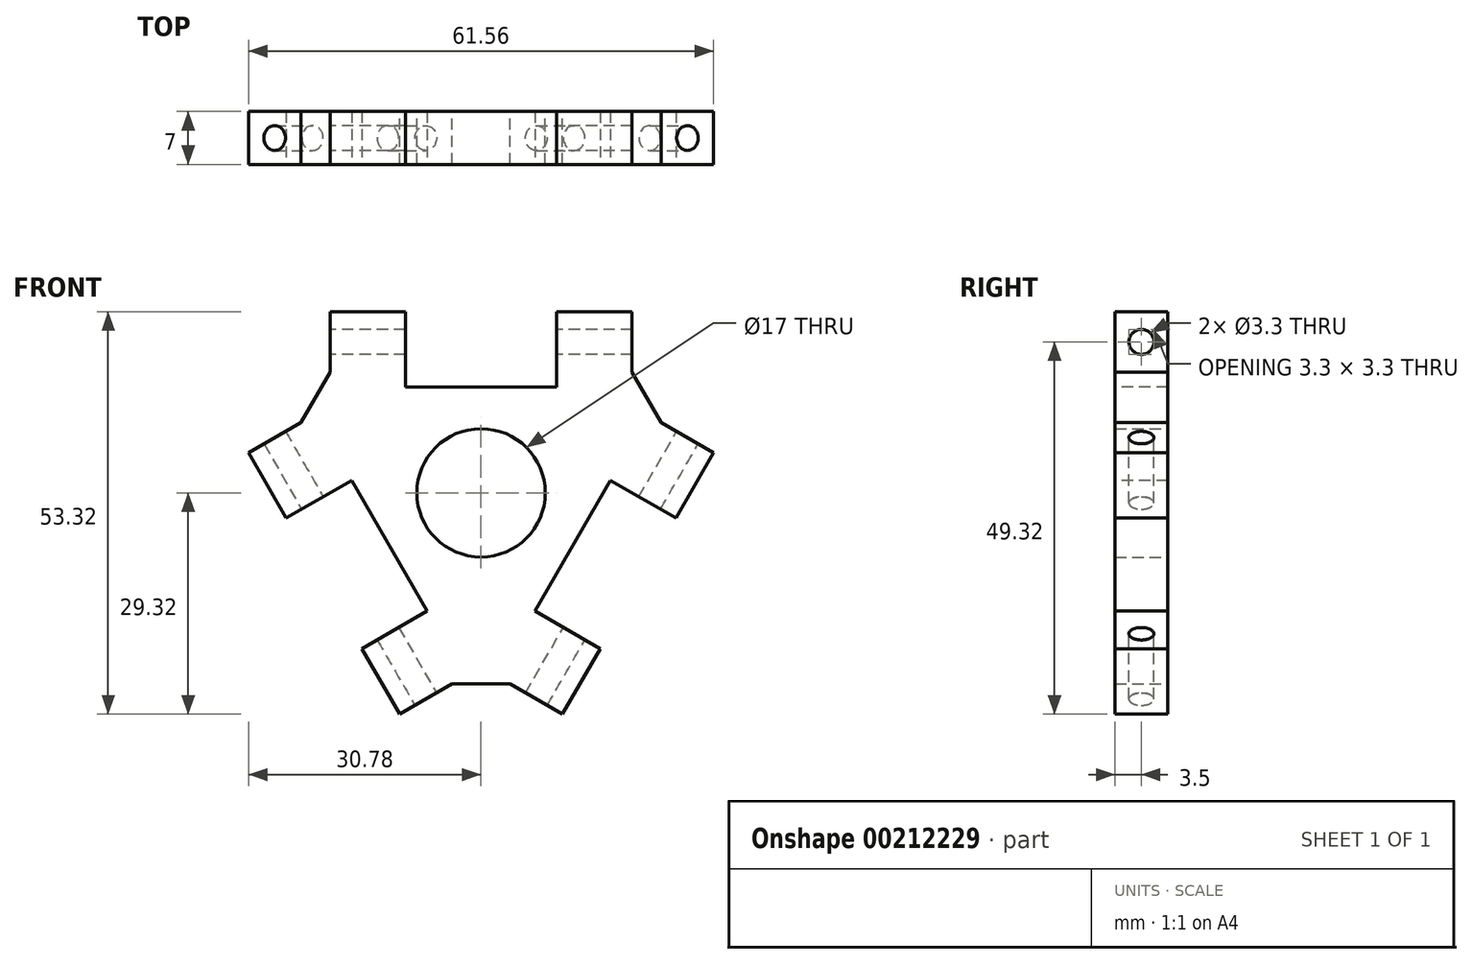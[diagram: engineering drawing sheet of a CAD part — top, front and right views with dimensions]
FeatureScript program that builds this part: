
annotation { "Feature Type Name" : "Feature", "Feature Type Description" : "" }
export const myFeature = defineFeature(function(context is Context, id is Id, definition is map)
    precondition{}
    {
        {
            var Q0;
            Q0=qCreatedBy(makeId("Front.planeOp"),FACE);
            var sketch = newSketch(context, id + "F0", { "sketchPlane" : qUnion([Q0])});
            skCircle(sketch, "E0", {"center": v(0, 0) * mm, "radius": 8.5 * mm});
            skCircle(sketch, "E1", {"center": v(0, 0) * mm, "radius": 16 * mm});
            skLineSegment(sketch, "E2", {"start": v(0, 0) * mm, "end": v(0, 20) * mm});
            skLineSegment(sketch, "E3", {"start": v(0, 0) * mm, "end": v(-17.32, -10) * mm});
            skLineSegment(sketch, "E4", {"start": v(0, 0) * mm, "end": v(17.32, -10) * mm});
            skPoint(sketch, "E5", {"position": v(0, 16) * mm});
            skPoint(sketch, "E6", {"position": v(-13.86, -8) * mm});
            skPoint(sketch, "E7", {"position": v(13.86, -8) * mm});
            skPoint(sketch, "E8", {"position": v(0, 20) * mm});
            skLineSegment(sketch, "E9.bottom", {"start": v(20, 16) * mm, "end": v(-20, 16) * mm});
            skLineSegment(sketch, "E9.top", {"start": v(20, 24) * mm, "end": v(-20, 24) * mm});
            skLineSegment(sketch, "E9.left", {"start": v(20, 16) * mm, "end": v(20, 24) * mm});
            skLineSegment(sketch, "E9.right", {"start": v(-20, 16) * mm, "end": v(-20, 24) * mm});
            skPoint(sketch, "E10", {"position": v(-17.32, -10) * mm});
            skPoint(sketch, "E11", {"position": v(17.32, -10) * mm});
            skLineSegment(sketch, "E12", {"start": v(-13.86, -8) * mm, "end": v(-23.86, 9.32) * mm});
            skLineSegment(sketch, "E13", {"start": v(-13.86, -8) * mm, "end": v(-3.86, -25.32) * mm});
            skLineSegment(sketch, "E14", {"start": v(-3.86, -25.32) * mm, "end": v(-10.78, -29.32) * mm});
            skLineSegment(sketch, "E15", {"start": v(-10.78, -29.32) * mm, "end": v(-30.78, 5.32) * mm});
            skLineSegment(sketch, "E16", {"start": v(-30.78, 5.32) * mm, "end": v(-23.86, 9.32) * mm});
            skLineSegment(sketch, "E17", {"start": v(13.86, -8) * mm, "end": v(23.86, 9.32) * mm});
            skLineSegment(sketch, "E18", {"start": v(23.86, 9.32) * mm, "end": v(30.78, 5.32) * mm});
            skLineSegment(sketch, "E19", {"start": v(30.78, 5.32) * mm, "end": v(10.78, -29.32) * mm});
            skLineSegment(sketch, "E20", {"start": v(10.78, -29.32) * mm, "end": v(3.86, -25.32) * mm});
            skLineSegment(sketch, "E21", {"start": v(20, 16) * mm, "end": v(23.86, 9.32) * mm});
            skLineSegment(sketch, "E22", {"start": v(3.86, -25.32) * mm, "end": v(-3.86, -25.32) * mm});
            skLineSegment(sketch, "E23", {"start": v(-20, 16) * mm, "end": v(-23.86, 9.32) * mm});
            skLineSegment(sketch, "E24", {"start": v(13.86, -8) * mm, "end": v(3.86, -25.32) * mm});
            skSolve(sketch);
        }
        {
            var Q0;
            {var subQ0=sQuery(id+"F0.wireOp",EDGE,"E3");var subQ1=sQuery(id+"F0.wireOp",EDGE,"E0");var subQ2=makeQuery(id+"F0.imprint","INTERSECT",VERTEX,{"derivedFrom":[subQ1,subQ0]});Q0=makeQuery(id+"F0.imprint","IMPRINT",FACE,{"disambiguationData":[TD([[makeQuery(id+"F0.imprint","IMPRINT",EDGE,{"disambiguationData":[TD([[subQ2,1.0]])],"derivedFrom":subQ1}),-1.0]])]});}
            var Q1;
            Q1=makeQuery(id+"F0.imprint","IMPRINT",FACE,{"disambiguationData":[TD([[makeQuery(id+"F0.imprint","IMPRINT",EDGE,{"derivedFrom":sQuery(id+"F0.wireOp",EDGE,"E9.top")}),1.0]])]});
            var Q2;
            {var subQ0=sQuery(id+"F0.wireOp",EDGE,"E12");Q2=makeQuery(id+"F0.imprint","IMPRINT",FACE,{"disambiguationData":[TD([[makeQuery(id+"F0.imprint","IMPRINT",EDGE,{"derivedFrom":subQ0}),-1.0]])]});}
            var Q3;
            Q3=makeQuery(id+"F0.imprint","IMPRINT",FACE,{"disambiguationData":[TD([[makeQuery(id+"F0.imprint","IMPRINT",EDGE,{"derivedFrom":sQuery(id+"F0.wireOp",EDGE,"E12")}),1.0]])]});
            var Q4;
            {var subQ0=sQuery(id+"F0.wireOp",EDGE,"E3");var subQ1=sQuery(id+"F0.wireOp",EDGE,"E0");var subQ2=makeQuery(id+"F0.imprint","INTERSECT",VERTEX,{"derivedFrom":[subQ1,subQ0]});Q4=makeQuery(id+"F0.imprint","IMPRINT",FACE,{"disambiguationData":[TD([[makeQuery(id+"F0.imprint","IMPRINT",EDGE,{"disambiguationData":[TD([[subQ2,-1.0]])],"derivedFrom":subQ1}),-1.0]])]});}
            var Q5;
            {var subQ0=sQuery(id+"F0.wireOp",EDGE,"E13");Q5=makeQuery(id+"F0.imprint","IMPRINT",FACE,{"disambiguationData":[TD([[makeQuery(id+"F0.imprint","IMPRINT",EDGE,{"derivedFrom":subQ0}),1.0]])]});}
            var Q6;
            Q6=makeQuery(id+"F0.imprint","IMPRINT",FACE,{"disambiguationData":[TD([[makeQuery(id+"F0.imprint","IMPRINT",EDGE,{"derivedFrom":sQuery(id+"F0.wireOp",EDGE,"E17")}),-1.0]])]});
            var Q7;
            {var subQ0=sQuery(id+"F0.wireOp",EDGE,"E2");var subQ1=sQuery(id+"F0.wireOp",EDGE,"E0");var subQ2=makeQuery(id+"F0.imprint","INTERSECT",VERTEX,{"derivedFrom":[subQ1,subQ0]});Q7=makeQuery(id+"F0.imprint","IMPRINT",FACE,{"disambiguationData":[TD([[makeQuery(id+"F0.imprint","IMPRINT",EDGE,{"disambiguationData":[TD([[subQ2,1.0]])],"derivedFrom":subQ1}),-1.0]])]});}
            var Q8;
            {var subQ0=sQuery(id+"F0.wireOp",EDGE,"E17");Q8=makeQuery(id+"F0.imprint","IMPRINT",FACE,{"disambiguationData":[TD([[makeQuery(id+"F0.imprint","IMPRINT",EDGE,{"derivedFrom":subQ0}),1.0]])]});}
            extrude(context, id + "F1", {"entities" : qUnion([Q0, Q1, Q2, Q3, Q4, Q5, Q6, Q7, Q8]), "depth" : 7 * mm});
        }
        {
            var Q0;
            Q0=makeQuery(id+"F1.opExtrude","CAP_FACE",FACE,{"disambiguationData":[OSD([sQuery(id+"F0.wireOp",EDGE,"E0"),sQuery(id+"F0.wireOp",EDGE,"E9.top"),sQuery(id+"F0.wireOp",EDGE,"E9.left"),sQuery(id+"F0.wireOp",EDGE,"E9.right"),sQuery(id+"F0.wireOp",EDGE,"E14"),sQuery(id+"F0.wireOp",EDGE,"E15"),sQuery(id+"F0.wireOp",EDGE,"E16"),sQuery(id+"F0.wireOp",EDGE,"E18"),sQuery(id+"F0.wireOp",EDGE,"E19"),sQuery(id+"F0.wireOp",EDGE,"E20"),sQuery(id+"F0.wireOp",EDGE,"E21"),sQuery(id+"F0.wireOp",EDGE,"E22"),sQuery(id+"F0.wireOp",EDGE,"E23")])],"isStart":false});
            var sketch = newSketch(context, id + "F2", { "sketchPlane" : qUnion([Q0])});
            skLineSegment(sketch, "E25.bottom", {"start": v(10, 14) * mm, "end": v(-10, 14) * mm});
            skLineSegment(sketch, "E25.top", {"start": v(10, 34) * mm, "end": v(-10, 34) * mm});
            skLineSegment(sketch, "E25.left", {"start": v(10, 14) * mm, "end": v(10, 34) * mm});
            skLineSegment(sketch, "E25.right", {"start": v(-10, 14) * mm, "end": v(-10, 34) * mm});
            skPoint(sketch, "E25.middle", {"position": v(0, 24) * mm});
            skSolve(sketch);
        }
        {
            var Q0;
            {var subQ0=sQuery(id+"F2.wireOp",EDGE,"E25.bottom");Q0=makeQuery(id+"F2.imprint","IMPRINT",FACE,{"disambiguationData":[TD([[makeQuery(id+"F2.imprint","IMPRINT",EDGE,{"derivedFrom":subQ0}),-1.0]])]});}
            extrude(context, id + "F3", {"entities" : qUnion([Q0]), "operationType" : NewBodyOperationType.REMOVE, "endBound" : BoundingType.THROUGH_ALL, "oppositeDirection" : true, "depth" : 25 * mm});
        }
        {
            var Q0;
            Q0=makeQuery(id+"F1.opExtrude","CAP_FACE",FACE,{"disambiguationData":[OSD([sQuery(id+"F0.wireOp",EDGE,"E0"),sQuery(id+"F0.wireOp",EDGE,"E9.top"),sQuery(id+"F0.wireOp",EDGE,"E9.left"),sQuery(id+"F0.wireOp",EDGE,"E9.right"),sQuery(id+"F0.wireOp",EDGE,"E14"),sQuery(id+"F0.wireOp",EDGE,"E15"),sQuery(id+"F0.wireOp",EDGE,"E16"),sQuery(id+"F0.wireOp",EDGE,"E18"),sQuery(id+"F0.wireOp",EDGE,"E19"),sQuery(id+"F0.wireOp",EDGE,"E20"),sQuery(id+"F0.wireOp",EDGE,"E21"),sQuery(id+"F0.wireOp",EDGE,"E22"),sQuery(id+"F0.wireOp",EDGE,"E23")])],"isStart":false});
            var sketch = newSketch(context, id + "F4", { "sketchPlane" : qUnion([Q0])});
            skLineSegment(sketch, "E26.bottom", {"start": v(24.44, -25.66) * mm, "end": v(7.12, -15.66) * mm});
            skLineSegment(sketch, "E26.top", {"start": v(34.44, -8.34) * mm, "end": v(17.12, 1.66) * mm});
            skLineSegment(sketch, "E26.left", {"start": v(24.44, -25.66) * mm, "end": v(34.44, -8.34) * mm});
            skLineSegment(sketch, "E26.right", {"start": v(7.12, -15.66) * mm, "end": v(17.12, 1.66) * mm});
            skPoint(sketch, "E26.middle", {"position": v(20.78, -12) * mm});
            skSolve(sketch);
        }
        {
            var Q0;
            {var subQ0=sQuery(id+"F4.wireOp",EDGE,"E26.right");Q0=makeQuery(id+"F4.imprint","IMPRINT",FACE,{"disambiguationData":[TD([[makeQuery(id+"F4.imprint","IMPRINT",EDGE,{"derivedFrom":subQ0}),-1.0]])]});}
            extrude(context, id + "F5", {"entities" : qUnion([Q0]), "operationType" : NewBodyOperationType.REMOVE, "endBound" : BoundingType.THROUGH_ALL, "oppositeDirection" : true, "depth" : 25 * mm});
        }
        {
            var Q0;
            Q0=makeQuery(id+"F1.opExtrude","CAP_FACE",FACE,{"disambiguationData":[OSD([sQuery(id+"F0.wireOp",EDGE,"E0"),sQuery(id+"F0.wireOp",EDGE,"E9.top"),sQuery(id+"F0.wireOp",EDGE,"E9.left"),sQuery(id+"F0.wireOp",EDGE,"E9.right"),sQuery(id+"F0.wireOp",EDGE,"E14"),sQuery(id+"F0.wireOp",EDGE,"E15"),sQuery(id+"F0.wireOp",EDGE,"E16"),sQuery(id+"F0.wireOp",EDGE,"E18"),sQuery(id+"F0.wireOp",EDGE,"E19"),sQuery(id+"F0.wireOp",EDGE,"E20"),sQuery(id+"F0.wireOp",EDGE,"E21"),sQuery(id+"F0.wireOp",EDGE,"E22"),sQuery(id+"F0.wireOp",EDGE,"E23")])],"isStart":false});
            var sketch = newSketch(context, id + "F6", { "sketchPlane" : qUnion([Q0])});
            skLineSegment(sketch, "E27.bottom", {"start": v(-7.12, -15.66) * mm, "end": v(-24.44, -25.66) * mm});
            skLineSegment(sketch, "E27.top", {"start": v(-17.12, 1.66) * mm, "end": v(-34.44, -8.34) * mm});
            skLineSegment(sketch, "E27.left", {"start": v(-7.12, -15.66) * mm, "end": v(-17.12, 1.66) * mm});
            skLineSegment(sketch, "E27.right", {"start": v(-24.44, -25.66) * mm, "end": v(-34.44, -8.34) * mm});
            skPoint(sketch, "E27.middle", {"position": v(-20.78, -12) * mm});
            skSolve(sketch);
        }
        {
            var Q0;
            {var subQ0=sQuery(id+"F6.wireOp",EDGE,"E27.left");Q0=makeQuery(id+"F6.imprint","IMPRINT",FACE,{"disambiguationData":[TD([[makeQuery(id+"F6.imprint","IMPRINT",EDGE,{"derivedFrom":subQ0}),1.0]])]});}
            extrude(context, id + "F7", {"entities" : qUnion([Q0]), "operationType" : NewBodyOperationType.REMOVE, "endBound" : BoundingType.THROUGH_ALL, "oppositeDirection" : true, "depth" : 25 * mm});
        }
        {
            var Q0;
            Q0=makeQuery(id+"F1.opExtrude","SWEPT_FACE",FACE,{"disambiguationData":[OSD([sQuery(id+"F0.wireOp",EDGE,"E9.right")])]});
            var sketch = newSketch(context, id + "F8", { "sketchPlane" : qUnion([Q0])});
            skLineSegment(sketch, "E28", {"start": v(7, 20) * mm, "end": v(0, 20) * mm});
            skPoint(sketch, "E29", {"position": v(3.5, 20) * mm});
            skSolve(sketch);
        }
        {
            var Q0;
            Q0=sQuery(id+"F8.wireOp",VERTEX,"E29");
            var Q1;
            Q1=makeQuery(id+"F1.opExtrude","SWEPT_BODY",BODY,{"disambiguationData":[OSD([sQuery(id+"F0.wireOp",EDGE,"E0"),sQuery(id+"F0.wireOp",EDGE,"E9.top"),sQuery(id+"F0.wireOp",EDGE,"E9.left"),sQuery(id+"F0.wireOp",EDGE,"E9.right"),sQuery(id+"F0.wireOp",EDGE,"E14"),sQuery(id+"F0.wireOp",EDGE,"E15"),sQuery(id+"F0.wireOp",EDGE,"E16"),sQuery(id+"F0.wireOp",EDGE,"E18"),sQuery(id+"F0.wireOp",EDGE,"E19"),sQuery(id+"F0.wireOp",EDGE,"E20"),sQuery(id+"F0.wireOp",EDGE,"E21"),sQuery(id+"F0.wireOp",EDGE,"E22"),sQuery(id+"F0.wireOp",EDGE,"E23")])]});
            hole(context, id + "F9", {"style" : HoleStyle.SIMPLE, "endStyle" : HoleEndStyle.THROUGH, "holeDiameter" : 3.3 * mm, "locations" : qUnion([Q0]), "scope" : qUnion([Q1]), "isTappedThrough" : true});
        }
        {
            var Q0;
            Q0=makeQuery(id+"F1.opExtrude","SWEPT_FACE",FACE,{"disambiguationData":[OSD([sQuery(id+"F0.wireOp",EDGE,"E18")])]});
            var sketch = newSketch(context, id + "F10", { "sketchPlane" : qUnion([Q0])});
            skLineSegment(sketch, "E30", {"start": v(20, 0) * mm, "end": v(20, -7) * mm});
            skPoint(sketch, "E31", {"position": v(20, -3.5) * mm});
            skSolve(sketch);
        }
        {
            var Q0;
            Q0=sQuery(id+"F10.wireOp",VERTEX,"E31");
            var Q1;
            Q1=makeQuery(id+"F1.opExtrude","SWEPT_BODY",BODY,{"disambiguationData":[OSD([sQuery(id+"F0.wireOp",EDGE,"E0"),sQuery(id+"F0.wireOp",EDGE,"E9.top"),sQuery(id+"F0.wireOp",EDGE,"E9.left"),sQuery(id+"F0.wireOp",EDGE,"E9.right"),sQuery(id+"F0.wireOp",EDGE,"E14"),sQuery(id+"F0.wireOp",EDGE,"E15"),sQuery(id+"F0.wireOp",EDGE,"E16"),sQuery(id+"F0.wireOp",EDGE,"E18"),sQuery(id+"F0.wireOp",EDGE,"E19"),sQuery(id+"F0.wireOp",EDGE,"E20"),sQuery(id+"F0.wireOp",EDGE,"E21"),sQuery(id+"F0.wireOp",EDGE,"E22"),sQuery(id+"F0.wireOp",EDGE,"E23")])]});
            hole(context, id + "F11", {"style" : HoleStyle.SIMPLE, "endStyle" : HoleEndStyle.THROUGH, "holeDiameter" : 3.3 * mm, "locations" : qUnion([Q0]), "scope" : qUnion([Q1]), "isTappedThrough" : true});
        }
        {
            var Q0;
            Q0=makeQuery(id+"F1.opExtrude","SWEPT_FACE",FACE,{"disambiguationData":[OSD([sQuery(id+"F0.wireOp",EDGE,"E14")])]});
            var sketch = newSketch(context, id + "F12", { "sketchPlane" : qUnion([Q0])});
            skLineSegment(sketch, "E32", {"start": v(-20, 7) * mm, "end": v(-20, 0) * mm});
            skPoint(sketch, "E33", {"position": v(-20, 3.5) * mm});
            skSolve(sketch);
        }
        {
            var Q0;
            Q0=sQuery(id+"F12.wireOp",VERTEX,"E33");
            var Q1;
            Q1=makeQuery(id+"F1.opExtrude","SWEPT_BODY",BODY,{"disambiguationData":[OSD([sQuery(id+"F0.wireOp",EDGE,"E0"),sQuery(id+"F0.wireOp",EDGE,"E9.top"),sQuery(id+"F0.wireOp",EDGE,"E9.left"),sQuery(id+"F0.wireOp",EDGE,"E9.right"),sQuery(id+"F0.wireOp",EDGE,"E14"),sQuery(id+"F0.wireOp",EDGE,"E15"),sQuery(id+"F0.wireOp",EDGE,"E16"),sQuery(id+"F0.wireOp",EDGE,"E18"),sQuery(id+"F0.wireOp",EDGE,"E19"),sQuery(id+"F0.wireOp",EDGE,"E20"),sQuery(id+"F0.wireOp",EDGE,"E21"),sQuery(id+"F0.wireOp",EDGE,"E22"),sQuery(id+"F0.wireOp",EDGE,"E23")])]});
            hole(context, id + "F13", {"style" : HoleStyle.SIMPLE, "endStyle" : HoleEndStyle.THROUGH, "holeDiameter" : 3.3 * mm, "locations" : qUnion([Q0]), "scope" : qUnion([Q1]), "isTappedThrough" : true});
        }
    });
